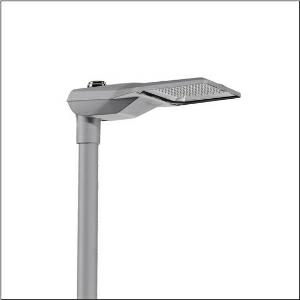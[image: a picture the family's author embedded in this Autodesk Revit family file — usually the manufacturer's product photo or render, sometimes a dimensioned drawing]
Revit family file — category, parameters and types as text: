
# Revit family: streetlight_sl_21_midi___st0_5a_5xe7b37n08mb_20a0
name_source: partatom
category: Lighting Fixtures
units: mm (PartAtom-declared; Revit-internal decimal feet)

## family parameters
Cut with Voids When Loaded = No
Host = Face
Light Source = No
Part Type = Normal
Room Calculation Point = No
Round Connector Dimension = Use Diameter
Shared = No

## types (1)
- --- (1 x LED, 18270 lm, 136 W, 3000K)
    Apparent Load = 136 VA
    CIE Flux Codes = 41 75 97 100 100
    Color Rendering = 70
    Color Temperature = 3000K
    Default Elevation = 1800 mm
    Description = Streetlight SL 21 midi, mast luminaire, primary light control with lens, of PMMA, primary optical cover: cover, of toughened safety glass, transparent, light distribution: ST0.5a, light emission: direct distribution, primary light characteristic: asymmetric, installation type: side-entry, LED, 3G 2.5mm², High Power LED, rated luminous flux: 18.270lm, luminous efficacy: 134lm/W, light colour: 730, colour temperature: 3000K, control gear: NEMA (7pin), control: overheat protection, pre-setting: linear dimming characteristic, constant luminous flux control, time-dependent luminous flux control, flexible luminous flux parameterisation, mains connection: 220..240V, AC, 50/60Hz, connection cable pre-assembled, cable length: 12,5m, wiring characteristics: H05VV-F, start of lifetime: 136W, end of service life: 142W, reduction: 61W, luminaire housing, of diecast aluminium (EN AC-44300), powder-coated, Siteco® metallic grey (DB 702S), corrosivity category C5 mid according to DIN EN ISO 12944, multi-level sealing system, sealing non-destructively replaceable, inclination adjustable: 0°, 5°, 10°, 15°, length: 644mm, width: 335mm, height: 110mm, spigot size: 42mm (side-entry), mounting height: 4..8m, protection rating (complete): IP66, insulation class (complete): insulation class I (protective earthing), certification: CE, ENEC, ENEC+, VDE, impact resistance: IK10, permissible operating ambient temperature for outdoor applications: -40..+50°C, standard-compliant lighting for roads and squares, packaging unit: 1 piece

Light Distribution: ST0.5a
    Height = 111 mm
    Lamp = 1 x LED
    Lamp Light Flux = 18270 lm
    Lamp Power = 136 W
    Lamp count = 1
    Length = 644 mm
    Luminous efficacy = 134 lm/W
    Manufacturer = Siteco
    ModVariant = No
    Model = 5XE7B37N08MB
    Number of Poles = 1
    OnlyDefault = Yes
    Power Factor = 1
    Product Name = Streetlight SL 21 midi | ST0.5a
    Product group = mast luminaire | pylon top
    ProductGroupID = 6100
    Protection Class = Protection class I
    Protection Degree = IP 66
    RLX_Detail_Level = 1
    RLX_Emergency_Light_Flux = 0 lm
    RLX_Emergency_Type = 0
    RLX_Emergency_Type_DB = No
    RlxData = <blob elided: 37561 chars, md5=d65ea511>
    Socket = socket
    Standby Power = 0 W
    System Light Flux = 18270 lm
    System Power = 136 W
    Type Comments = factory setting: luminous flux: 100 % | dim-lin: 254 | 695 mA
    Type Image = l_1294377.jpg
    URL = http://relux.com
    VarID = @adj_137340
    Voltage = 0 V
    Weight = 0.00 kg
    Width = 336 mm

## geometry (parser evidence)
native form markers: Blend x4, Sweep x11
no freeform markers — native parametric forms only
